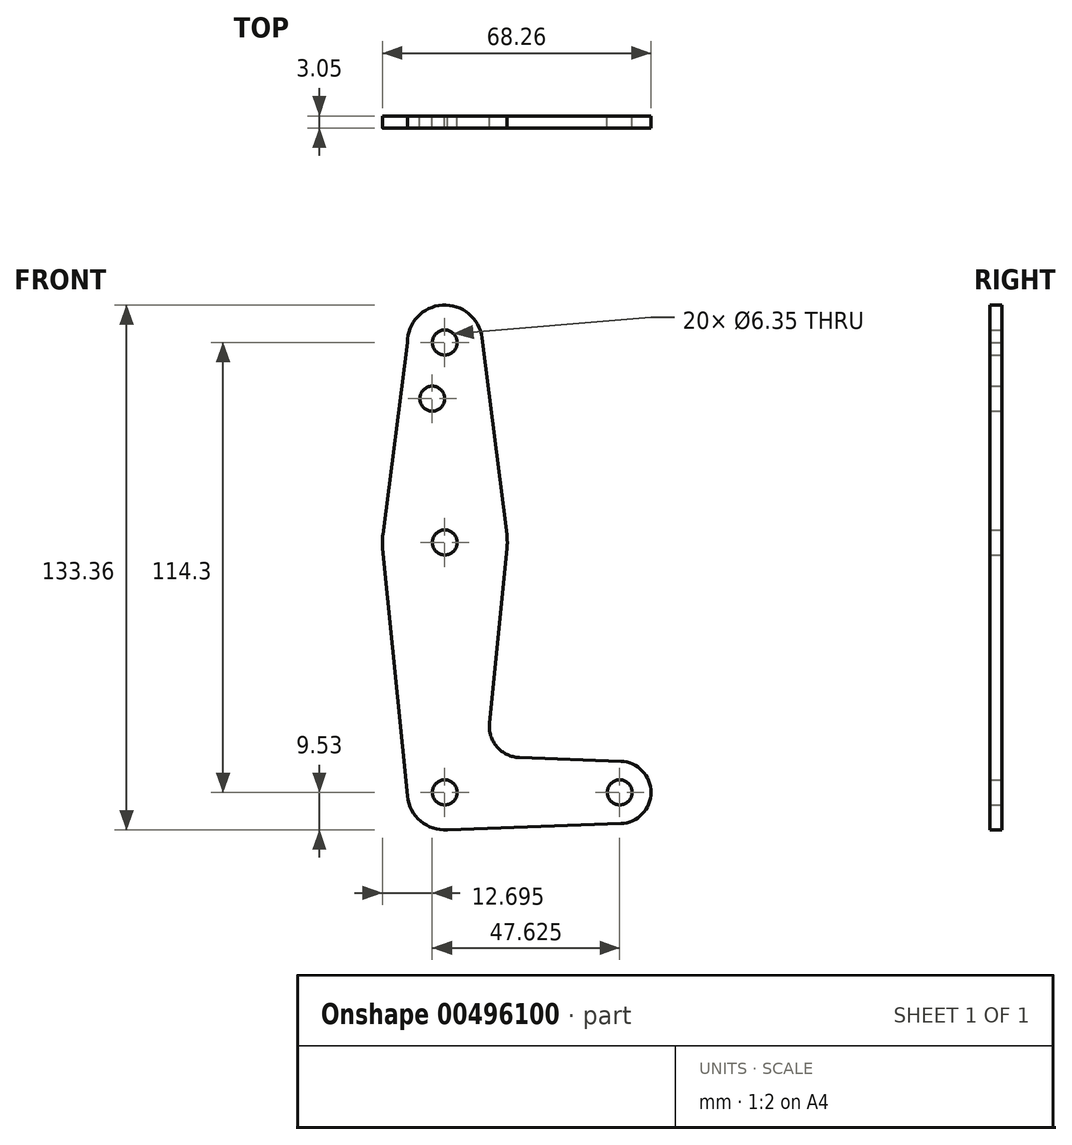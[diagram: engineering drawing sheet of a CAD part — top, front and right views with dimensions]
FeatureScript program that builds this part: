
annotation { "Feature Type Name" : "Feature", "Feature Type Description" : "" }
export const myFeature = defineFeature(function(context is Context, id is Id, definition is map)
    precondition{}
    {
        {
            var Q0;
            Q0=qCreatedBy(makeId("Front.planeOp"),FACE);
            var sketch = newSketch(context, id + "F0", { "sketchPlane" : qUnion([Q0])});
            skLineSegment(sketch, "E0", {"start": v(0, 0) * mm, "end": v(0, 114.3) * mm, "construction": true});
            skLineSegment(sketch, "E1", {"start": v(0, 0) * mm, "end": v(44.45, 0) * mm, "construction": true});
            skCircle(sketch, "E2", {"center": v(0, 114.3) * mm, "radius": 9.53 * mm});
            skCircle(sketch, "E3", {"center": v(0, 63.5) * mm, "radius": 15.88 * mm});
            skCircle(sketch, "E4", {"center": v(0, 0) * mm, "radius": 9.53 * mm});
            skCircle(sketch, "E5", {"center": v(44.45, 0) * mm, "radius": 7.94 * mm});
            skCircle(sketch, "E6", {"center": v(0, 114.3) * mm, "radius": 3.18 * mm});
            skCircle(sketch, "E7", {"center": v(-3.18, 100.03) * mm, "radius": 3.18 * mm});
            skCircle(sketch, "E8", {"center": v(0, 0) * mm, "radius": 3.18 * mm});
            skCircle(sketch, "E9", {"center": v(44.45, 0) * mm, "radius": 3.18 * mm});
            skLineSegment(sketch, "E10", {"start": v(9.45, 115.5) * mm, "end": v(15.75, 65.48) * mm});
            skLineSegment(sketch, "E11", {"start": v(-15.8, 61.91) * mm, "end": v(-9.48, -0.95) * mm});
            skLineSegment(sketch, "E12", {"start": v(15.8, 61.91) * mm, "end": v(11.34, 17.6) * mm});
            skLineSegment(sketch, "E13", {"start": v(-9.53, 114.3) * mm, "end": v(-15.75, 65.5) * mm});
            skCircle(sketch, "E14", {"center": v(0, 63.5) * mm, "radius": 3.18 * mm});
            skLineSegment(sketch, "E15", {"start": v(18.97, 8.85) * mm, "end": v(44.73, 7.93) * mm});
            skLineSegment(sketch, "E16", {"start": v(0, -9.53) * mm, "end": v(44.73, -7.93) * mm});
            skArc(sketch, "E17.filletArc", {"start": v(11.34, 17.6) * mm, "mid": v(13.26, 11.57) * mm, "end": v(18.97, 8.85) * mm});
            skSolve(sketch);
        }
        {
            var Q0;
            Q0 = qSketchRegion(id + "F0", true);
            extrude(context, id + "F1", {"entities" : qUnion([Q0]), "depth" : 3.05 * mm});
        }
    });
